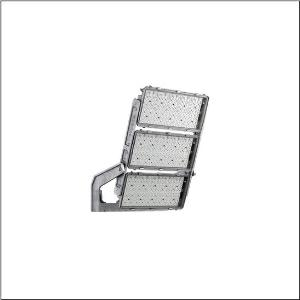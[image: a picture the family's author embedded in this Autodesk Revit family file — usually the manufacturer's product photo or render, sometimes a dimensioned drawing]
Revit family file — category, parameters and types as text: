
# Revit family: floodlight_fl_11_maxi_pro_remote___pl52_5xa779427d01aa_0793
name_source: partatom
category: Lighting Fixtures
units: mm (PartAtom-declared; Revit-internal decimal feet)

## family parameters
Cut with Voids When Loaded = No
Host = Face
Light Source = No
Part Type = Normal
Room Calculation Point = No
Round Connector Dimension = Use Diameter
Shared = No

## types (1)
- --- (1 x LED, 173640 lm, 1425.5 W, 5000K)
    Apparent Load = 1425 VA
    CIE Flux Codes = 24 55 98 100 100
    Color Rendering = 70
    Color Temperature = 5000K
    Default Elevation = 1800 mm
    Description = Floodlight FL 11  maxi  pro Remote floodlight; light control with lens of PMMA; cover panel of toughened safety glass, transparent; light distribution: PL52, asymmetric direct distribution, LEDcolour temperature: 5000K, rated luminous flux: 173.640lm, colour rendering: CRI > 70, light colour: 750; luminous efficacy: 122lm/W; brightness control: DALI 2 (1 DALI address); with terminal, 8-pole, max. 2.5mm², mains connection: 220..240V/380..400V AC, 50/60Hz, surge voltage resistance: line to ground: 10kV, ECG replaceable separately, LED unit replaceable without ESD environment, dustproof LED module, dimming range 10..100%, no afterglow with DALI off / DMX off command; 1426W floodlight with 3x LED unit of diecast aluminium, coated grey; length: 713mm / width: 651mm / height: 338mm; mounting bracket, of diecast aluminium, uncoated, natural, equipment: Power, protection rating (complete): IP66; insulation class (complete): insulation class I (protective earthing); certification: CE, ENEC, VDE; ball protection: ball impact resistance with accessories, impact resistance: IK07; rated ambient temperature 10°C, only for outdoor installations, permissible operating ambient temperature: -40..+30°C, permissible storage temperature: -40..+85°C; packaging unit: 1 piece

Light Distribution: PL52
    Height = 320 mm
    Lamp = 1 x LED
    Lamp Light Flux = 173640 lm
    Lamp Power = 1425.5 W
    Lamp count = 1
    Length = 1002 mm
    Luminous efficacy = 122 lm/W
    Manufacturer = Siteco
    ModVariant = No
    Model = 5XA779427D01AA
    Mounting Place = Ceiling
    Mounting Type = Surface mounted
    Number of Poles = 1
    OnlyDefault = Yes
    Power Factor = 1
    Product Name = Floodlight FL 11 maxi pro Remote | PL52
    Product group = floodlight | ceiling mounted
    ProductGroupID = 302
    Protection Class = Protection class I
    Protection Degree = IP 66
    RLX_Detail_Level = 1
    RLX_Emergency_Light_Flux = 0 lm
    RLX_Emergency_Type = 0
    RLX_Emergency_Type_DB = No
    RlxData = <blob elided: 52617 chars, md5=7799a80c>
    Socket = socket
    Standby Power = 0 W
    System Light Flux = 173640 lm
    System Power = 1425 W
    Type Comments = factory setting: luminous flux: 100 % | dim-lin: 254 | 980 mA
    Type Image = l_1006784.jpg
    URL = http://relux.com
    VarID = @adj_028275
    Voltage = 0 V
    Weight = 0.00 kg
    Width = 655 mm

## geometry (parser evidence)
native form markers: Blend x4, Sweep x13
no freeform markers — native parametric forms only
